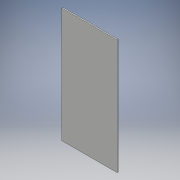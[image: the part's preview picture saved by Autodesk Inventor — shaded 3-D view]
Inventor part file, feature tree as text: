
AUTODESK INVENTOR PART (.ipt)
format: ipt  version: 2018 (Build 220112000, 112)  size: 90,624 bytes
history: native  units: mm
features: other x1, extrude x1, sketch x1
ambient origin geometry x8: Origin, YZ Plane, XZ Plane, XY Plane, X Axis, Y Axis, Z Axis, Center Point
bodies: Body1 (feature_tree)
feature tree (3):
  other  "ソリッド1"
  extrude  "押し出し1"  Depth=455.466667mm
  sketch  "スケッチ1"
